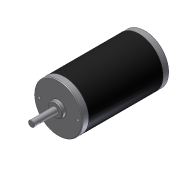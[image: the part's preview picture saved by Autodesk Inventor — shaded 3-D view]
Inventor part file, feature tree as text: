
AUTODESK INVENTOR PART (.ipt)
format: ipt  version: 2012 (Build 160160000, 160)  size: 137,216 bytes
history: native  units: in
note: dims shown in document units (in); Inventor stores cm internally (conversion verified against a paired STEP export)
features: chamfer x1, other x1, imported_body x1
ambient origin geometry x8: Origin, YZ Plane, XZ Plane, XY Plane, X Axis, Y Axis, Z Axis, Center Point
feature tree (3):
  chamfer  "Chamfer1"  [1 undecoded]
  other  "217-2000 - CIM Motor1"
  imported_body  "Base1"
note: 1 required parameter value undecoded (feature->parameter linkage not recoverable at this tier; creation-order binding heuristic only, values carry confidence <= 0.55)
